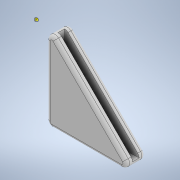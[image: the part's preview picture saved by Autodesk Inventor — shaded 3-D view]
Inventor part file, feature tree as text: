
AUTODESK INVENTOR PART (.ipt)
format: ipt  version: 2021.2 (Build 252289000, 289)  size: 147,968 bytes
history: native  units: in
note: dims shown in document units (in); Inventor stores cm internally (conversion verified against a paired STEP export)
features: fillet x3, extrude x2, sketch x2
ambient origin geometry x8: Origin, YZ Plane, XZ Plane, XY Plane, X Axis, Y Axis, Z Axis, Center Point
bodies: Solid1 (feature_tree)
feature tree (7):
  extrude  "Extrusion1"  Depth=0.23in
  extrude  "Extrusion2"  Depth=0.06in
  fillet  "Fillet1"  Radius=0.06in
  fillet  "Fillet2"  Radius=0.08in
  fillet  "Fillet3"  [1 undecoded]
  sketch  "Sketch1"  dims[d0=1.05in d1=0.23in]
  sketch  "Sketch3"  dims[d2=0.0in d3=0.06in d4=0.06in d5=0.08in d6=0.0in d7=0.06in d8=0.04in d9=0.04in]
note: 1 required parameter value undecoded (feature->parameter linkage not recoverable at this tier; creation-order binding heuristic only, values carry confidence <= 0.55)
